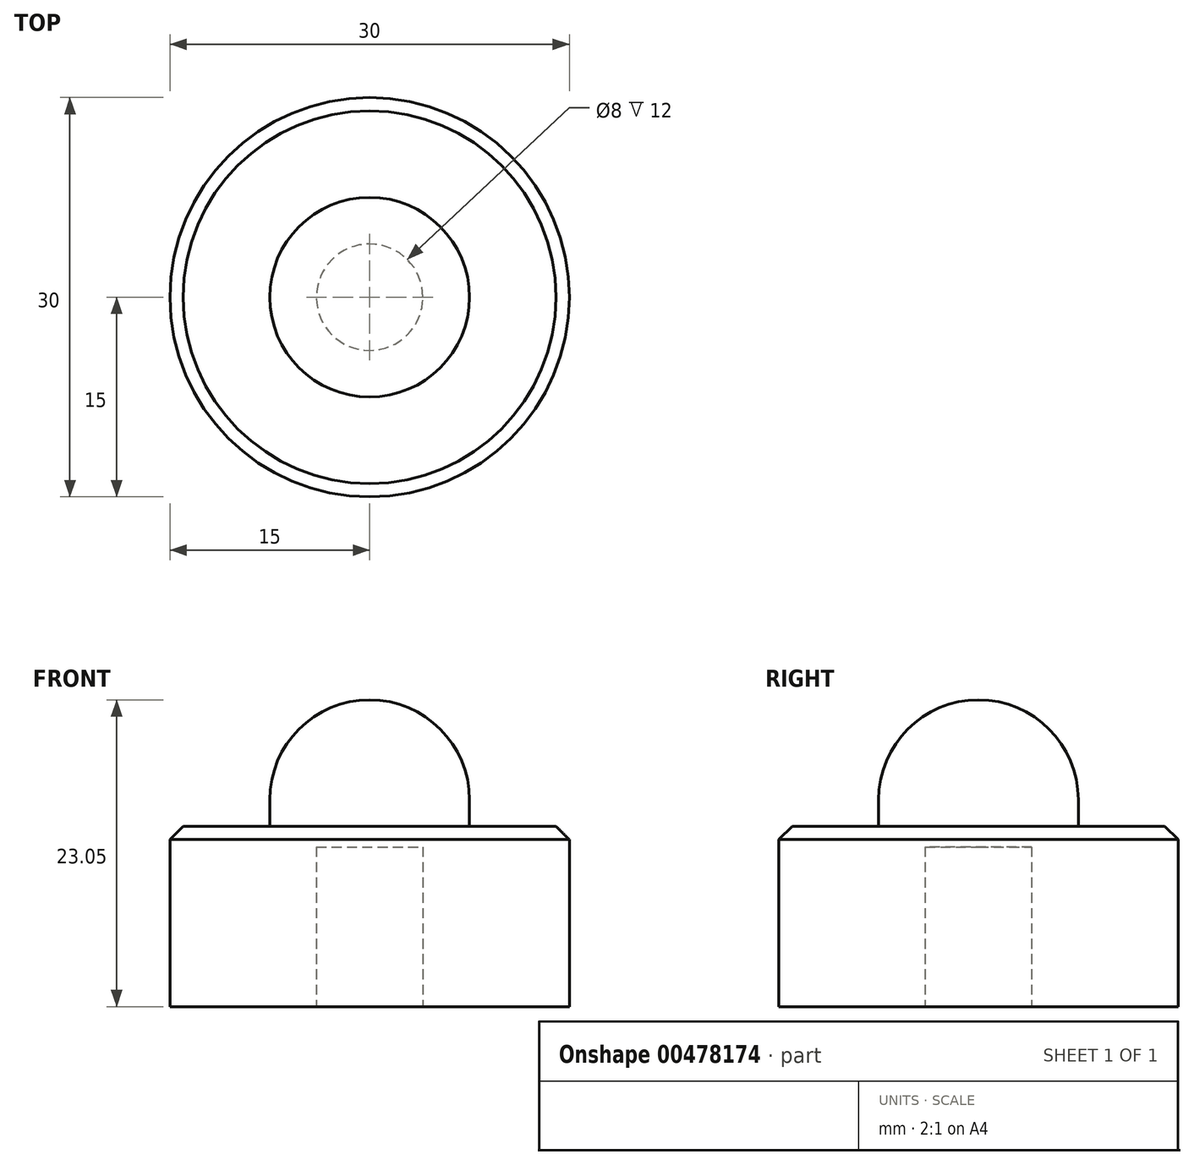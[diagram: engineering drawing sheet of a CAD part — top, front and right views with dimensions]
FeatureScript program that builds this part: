
annotation { "Feature Type Name" : "Feature", "Feature Type Description" : "" }
export const myFeature = defineFeature(function(context is Context, id is Id, definition is map)
    precondition{}
    {
        {
            var Q0;
            Q0=qCreatedBy(makeId("Top.planeOp"),FACE);
            var sketch = newSketch(context, id + "F0", { "sketchPlane" : qUnion([Q0])});
            skCircle(sketch, "E0", {"center": v(0, 0) * mm, "radius": 15 * mm});
            skSolve(sketch);
        }
        {
            var Q0;
            Q0=makeQuery(id+"F0.imprint","IMPRINT",FACE,{"disambiguationData":[TD([[makeQuery(id+"F0.imprint","IMPRINT",EDGE,{"derivedFrom":sQuery(id+"F0.wireOp",EDGE,"E0")}),1.0]])]});
            extrude(context, id + "F1", {"entities" : qUnion([Q0]), "depth" : 13.55 * mm});
        }
        {
            var Q0;
            Q0=makeQuery(id+"F1.opExtrude","CAP_FACE",FACE,{"disambiguationData":[OSD([sQuery(id+"F0.wireOp",EDGE,"E0")])],"isStart":false});
            var sketch = newSketch(context, id + "F2", { "sketchPlane" : qUnion([Q0])});
            skCircle(sketch, "E1", {"center": v(0, 0) * mm, "radius": 7.5 * mm});
            skSolve(sketch);
        }
        {
            var Q0;
            Q0 = qSketchRegion(id + "F2", true);
            extrude(context, id + "F3", {"entities" : qUnion([Q0]), "operationType" : NewBodyOperationType.ADD, "depth" : 2 * mm});
        }
        {
            var Q0;
            Q0=makeQuery(id+"F3.opExtrude","CAP_FACE",FACE,{"disambiguationData":[OSD([sQuery(id+"F2.wireOp",EDGE,"E1")])],"isStart":false});
            var sketch = newSketch(context, id + "F4", { "sketchPlane" : qUnion([Q0])});
            skLineSegment(sketch, "E2", {"start": v(0, -7.5) * mm, "end": v(0, 7.5) * mm});
            skPoint(sketch, "E3", {"position": v(0, 0) * mm});
            skArc(sketch, "E4", {"start": v(0, 7.5) * mm, "mid": v(7.5, 0) * mm, "end": v(0, -7.5) * mm});
            skSolve(sketch);
        }
        {
            var Q0;
            Q0=makeQuery(id+"F4.imprint","IMPRINT",FACE,{"disambiguationData":[TD([[makeQuery(id+"F4.imprint","IMPRINT",EDGE,{"derivedFrom":sQuery(id+"F4.wireOp",EDGE,"E2")}),-1.0]])]});
            var Q1;
            Q1=sQuery(id+"F4.wireOp",EDGE,"E2");
            revolve(context, id + "F5", {"operationType" : NewBodyOperationType.ADD, "entities" : qUnion([Q0]), "axis" : qUnion([Q1]), "revolveType" : RevolveType.ONE_DIRECTION, "oppositeDirection" : true, "angle" : 180 * degree});
        }
        {
            var Q0;
            Q0=makeQuery(id+"F1.opExtrude","CAP_FACE",FACE,{"disambiguationData":[OSD([sQuery(id+"F0.wireOp",EDGE,"E0")])],"isStart":true});
            var sketch = newSketch(context, id + "F6", { "sketchPlane" : qUnion([Q0])});
            skCircle(sketch, "E5", {"center": v(0, 0) * mm, "radius": 4 * mm});
            skSolve(sketch);
        }
        {
            var Q0;
            Q0 = qSketchRegion(id + "F6", true);
            extrude(context, id + "F7", {"entities" : qUnion([Q0]), "operationType" : NewBodyOperationType.REMOVE, "oppositeDirection" : true, "depth" : 12 * mm});
        }
        {
            var Q0;
            Q0=makeQuery(id+"F1.opExtrude","CAP_EDGE",EDGE,{"disambiguationData":[OSD([sQuery(id+"F0.wireOp",EDGE,"E0")])],"isStart":false});
            chamfer(context, id + "F8", {"entities" : qUnion([Q0]), "width" : 1 * mm, "tangentPropagation" : true});
        }
    });
